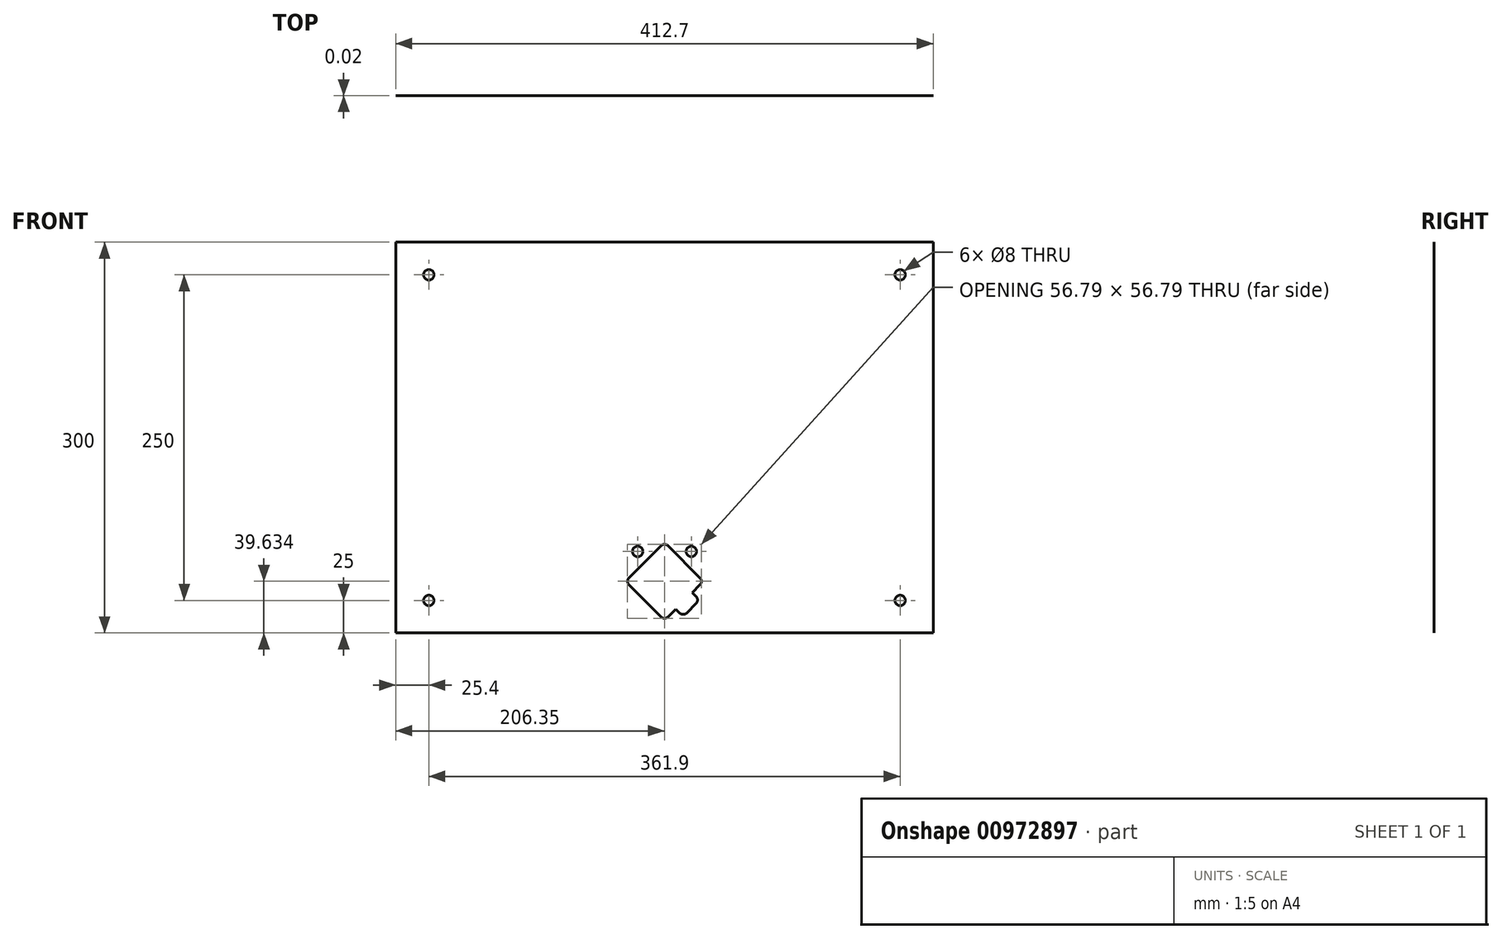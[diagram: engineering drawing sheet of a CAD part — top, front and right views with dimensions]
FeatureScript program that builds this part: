
annotation { "Feature Type Name" : "Feature", "Feature Type Description" : "" }
export const myFeature = defineFeature(function(context is Context, id is Id, definition is map)
    precondition{}
    {
        {
            var Q0;
            Q0=qCreatedBy(makeId("Front.planeOp"),FACE);
            var sketch = newSketch(context, id + "F0", { "sketchPlane" : qUnion([Q0])});
            skCircle(sketch, "E0", {"center": v(180.95, -125) * mm, "radius": 4 * mm});
            skCircle(sketch, "E1", {"center": v(-180.95, -125) * mm, "radius": 4 * mm});
            skCircle(sketch, "E2", {"center": v(-180.95, 125) * mm, "radius": 4 * mm});
            skCircle(sketch, "E3", {"center": v(180.95, 125) * mm, "radius": 4 * mm});
            skCircle(sketch, "E4", {"center": v(-20.6, -87.47) * mm, "radius": 4 * mm});
            skCircle(sketch, "E5", {"center": v(20.6, -87.47) * mm, "radius": 4 * mm});
            skLineSegment(sketch, "E6", {"start": v(-27.22, -107.54) * mm, "end": v(-2.83, -83.14) * mm});
            skLineSegment(sketch, "E7", {"start": v(206.35, 150) * mm, "end": v(-206.35, 150) * mm});
            skLineSegment(sketch, "E8", {"start": v(206.35, -150) * mm, "end": v(206.35, 150) * mm});
            skLineSegment(sketch, "E9", {"start": v(206.35, -150) * mm, "end": v(-206.35, -150) * mm});
            skLineSegment(sketch, "E10", {"start": v(-206.35, -150) * mm, "end": v(-206.35, 150) * mm});
            skLineSegment(sketch, "E11", {"start": v(-27.22, -113.2) * mm, "end": v(-2.83, -137.59) * mm});
            skLineSegment(sketch, "E12", {"start": v(2.83, -137.59) * mm, "end": v(8.66, -131.76) * mm});
            skLineSegment(sketch, "E13", {"start": v(8.66, -131.76) * mm, "end": v(11.5, -134.58) * mm});
            skLineSegment(sketch, "E14", {"start": v(24.22, -127.51) * mm, "end": v(17.15, -134.58) * mm});
            skLineSegment(sketch, "E15", {"start": v(21.39, -119.03) * mm, "end": v(24.22, -121.86) * mm});
            skLineSegment(sketch, "E16", {"start": v(27.22, -113.2) * mm, "end": v(21.39, -119.03) * mm});
            skLineSegment(sketch, "E17", {"start": v(2.83, -83.14) * mm, "end": v(27.22, -107.54) * mm});
            skArc(sketch, "E18", {"start": v(-27.22, -107.54) * mm, "mid": v(-28.4, -110.37) * mm, "end": v(-27.22, -113.2) * mm});
            skArc(sketch, "E19", {"start": v(-2.83, -137.59) * mm, "mid": v(0, -138.76) * mm, "end": v(2.83, -137.59) * mm});
            skArc(sketch, "E20", {"start": v(11.5, -134.58) * mm, "mid": v(14.32, -135.76) * mm, "end": v(17.15, -134.58) * mm});
            skArc(sketch, "E21", {"start": v(24.22, -127.51) * mm, "mid": v(25.39, -124.69) * mm, "end": v(24.22, -121.86) * mm});
            skArc(sketch, "E22", {"start": v(27.22, -113.2) * mm, "mid": v(28.4, -110.37) * mm, "end": v(27.22, -107.54) * mm});
            skArc(sketch, "E23", {"start": v(2.83, -83.14) * mm, "mid": v(0, -81.97) * mm, "end": v(-2.83, -83.14) * mm});
            skSolve(sketch);
        }
        {
            var Q0;
            Q0=qSketchRegion(id+"F0",true);
            extrude(context, id + "F1", {"entities" : qUnion([Q0]), "depth" : 1 / 50.8 * mm, "offsetDistance" : 25 * mm});
        }
    });
